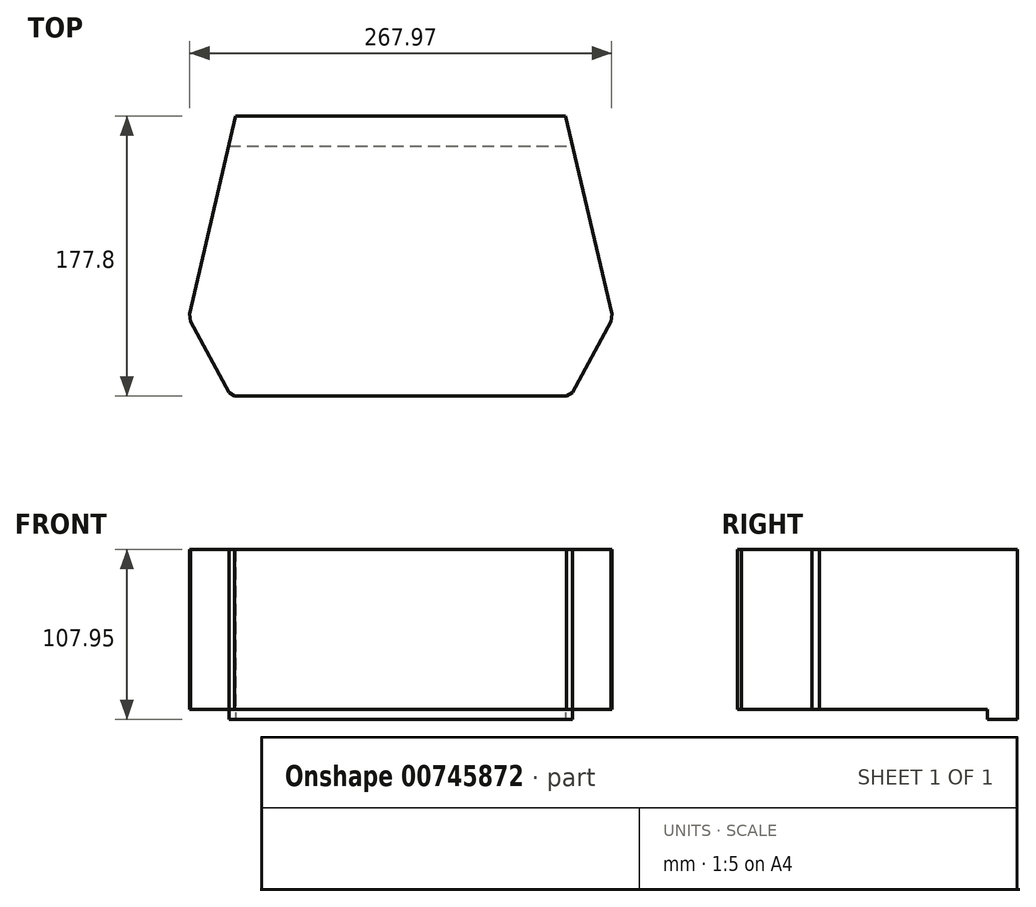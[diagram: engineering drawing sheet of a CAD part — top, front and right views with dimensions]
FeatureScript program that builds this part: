
annotation { "Feature Type Name" : "Feature", "Feature Type Description" : "" }
export const myFeature = defineFeature(function(context is Context, id is Id, definition is map)
    precondition{}
    {
        {
            var Q0;
            Q0=qCreatedBy(makeId("Top.planeOp"),FACE);
            var sketch = newSketch(context, id + "F0", { "sketchPlane" : qUnion([Q0])});
            skLineSegment(sketch, "E0", {"start": v(-153.63, -90.08) * mm, "end": v(138.47, -90.08) * mm});
            skLineSegment(sketch, "E1", {"start": v(138.47, -90.08) * mm, "end": v(97.2, 87.72) * mm});
            skLineSegment(sketch, "E2", {"start": v(97.2, 87.72) * mm, "end": v(-112.35, 87.72) * mm});
            skLineSegment(sketch, "E3", {"start": v(-112.35, 87.72) * mm, "end": v(-153.63, -90.08) * mm});
            skSolve(sketch);
        }
        {
            var Q0;
            Q0=makeQuery(id+"F0.imprint","IMPRINT",FACE,{"disambiguationData":[TD([[makeQuery(id+"F0.imprint","IMPRINT",EDGE,{"derivedFrom":sQuery(id+"F0.wireOp",EDGE,"E0")}),1.0]])]});
            extrude(context, id + "F1", {"entities" : qUnion([Q0]), "depth" : 107.95 * mm, "offsetDistance" : 25.4 * mm});
        }
        {
            var Q0;
            Q0=makeQuery(id+"F1.opExtrude","CAP_FACE",FACE,{"disambiguationData":[OSD([sQuery(id+"F0.wireOp",EDGE,"E0"),sQuery(id+"F0.wireOp",EDGE,"E1"),sQuery(id+"F0.wireOp",EDGE,"E2"),sQuery(id+"F0.wireOp",EDGE,"E3")])],"isStart":true});
            var sketch = newSketch(context, id + "F2", { "sketchPlane" : qUnion([Q0])});
            skLineSegment(sketch, "E4", {"start": v(-153.63, 90.08) * mm, "end": v(138.47, 90.08) * mm});
            skLineSegment(sketch, "E5", {"start": v(-116.77, -68.67) * mm, "end": v(101.62, -68.67) * mm});
            skLineSegment(sketch, "E6", {"start": v(138.47, 90.08) * mm, "end": v(101.62, -68.67) * mm});
            skLineSegment(sketch, "E7", {"start": v(-153.63, 90.08) * mm, "end": v(-116.77, -68.67) * mm});
            skSolve(sketch);
        }
        {
            var Q0;
            Q0=qSketchRegion(id+"F2",true);
            extrude(context, id + "F3", {"entities" : qUnion([Q0]), "operationType" : NewBodyOperationType.REMOVE, "oppositeDirection" : true, "depth" : 6.35 * mm, "offsetDistance" : 25.4 * mm});
        }
        {
            var Q0;
            Q0=makeQuery(id+"F1.opExtrude","SWEPT_EDGE",EDGE,{"disambiguationData":[OSD([sQuery(id+"F0.wireOp",EDGE,"E0"),sQuery(id+"F0.wireOp",EDGE,"E1")])]});
            var Q1;
            Q1=makeQuery(id+"F1.opExtrude","SWEPT_EDGE",EDGE,{"disambiguationData":[OSD([sQuery(id+"F0.wireOp",EDGE,"E0"),sQuery(id+"F0.wireOp",EDGE,"E3")])]});
            chamfer(context, id + "F4", {"entities" : qUnion([Q0, Q1]), "chamferType" : ChamferType.TWO_OFFSETS, "width1" : 38.1 * mm, "oppositeDirection" : false, "width2" : 50.8 * mm, "tangentPropagation" : true});
        }
        {
            var Q0;
            {var subQ0=sQuery(id+"F0.wireOp",EDGE,"E0");Q0=makeQuery(id+"F4.opChamfer","BLEND_EDGE",EDGE,{"blendedFrom":[makeQuery(id+"F1.opExtrude","SWEPT_EDGE",EDGE,{"disambiguationData":[OSD([subQ0,sQuery(id+"F0.wireOp",EDGE,"E1")])]}),makeQuery(id+"F1.opExtrude","SWEPT_FACE",FACE,{"disambiguationData":[OSD([subQ0])]})],"blendedInto":[makeQuery(id+"F1.opExtrude","SWEPT_FACE",FACE,{"disambiguationData":[OSD([subQ0])]})]});}
            var Q1;
            {var subQ0=sQuery(id+"F0.wireOp",EDGE,"E1");Q1=makeQuery(id+"F4.opChamfer","BLEND_EDGE",EDGE,{"blendedFrom":[makeQuery(id+"F1.opExtrude","SWEPT_EDGE",EDGE,{"disambiguationData":[OSD([sQuery(id+"F0.wireOp",EDGE,"E0"),subQ0])]}),makeQuery(id+"F1.opExtrude","SWEPT_FACE",FACE,{"disambiguationData":[OSD([subQ0])]})],"blendedInto":[makeQuery(id+"F1.opExtrude","SWEPT_FACE",FACE,{"disambiguationData":[OSD([subQ0])]})]});}
            var Q2;
            {var subQ0=sQuery(id+"F0.wireOp",EDGE,"E0");Q2=makeQuery(id+"F4.opChamfer","BLEND_EDGE",EDGE,{"blendedFrom":[makeQuery(id+"F1.opExtrude","SWEPT_EDGE",EDGE,{"disambiguationData":[OSD([subQ0,sQuery(id+"F0.wireOp",EDGE,"E3")])]}),makeQuery(id+"F1.opExtrude","SWEPT_FACE",FACE,{"disambiguationData":[OSD([subQ0])]})],"blendedInto":[makeQuery(id+"F1.opExtrude","SWEPT_FACE",FACE,{"disambiguationData":[OSD([subQ0])]})]});}
            var Q3;
            {var subQ0=sQuery(id+"F0.wireOp",EDGE,"E3");Q3=makeQuery(id+"F4.opChamfer","BLEND_EDGE",EDGE,{"blendedFrom":[makeQuery(id+"F1.opExtrude","SWEPT_EDGE",EDGE,{"disambiguationData":[OSD([sQuery(id+"F0.wireOp",EDGE,"E0"),subQ0])]}),makeQuery(id+"F1.opExtrude","SWEPT_FACE",FACE,{"disambiguationData":[OSD([subQ0])]})],"blendedInto":[makeQuery(id+"F1.opExtrude","SWEPT_FACE",FACE,{"disambiguationData":[OSD([subQ0])]})]});}
            chamfer(context, id + "F5", {"entities" : qUnion([Q0, Q1, Q2, Q3]), "width" : 2.54 * mm, "tangentPropagation" : true});
        }
    });
